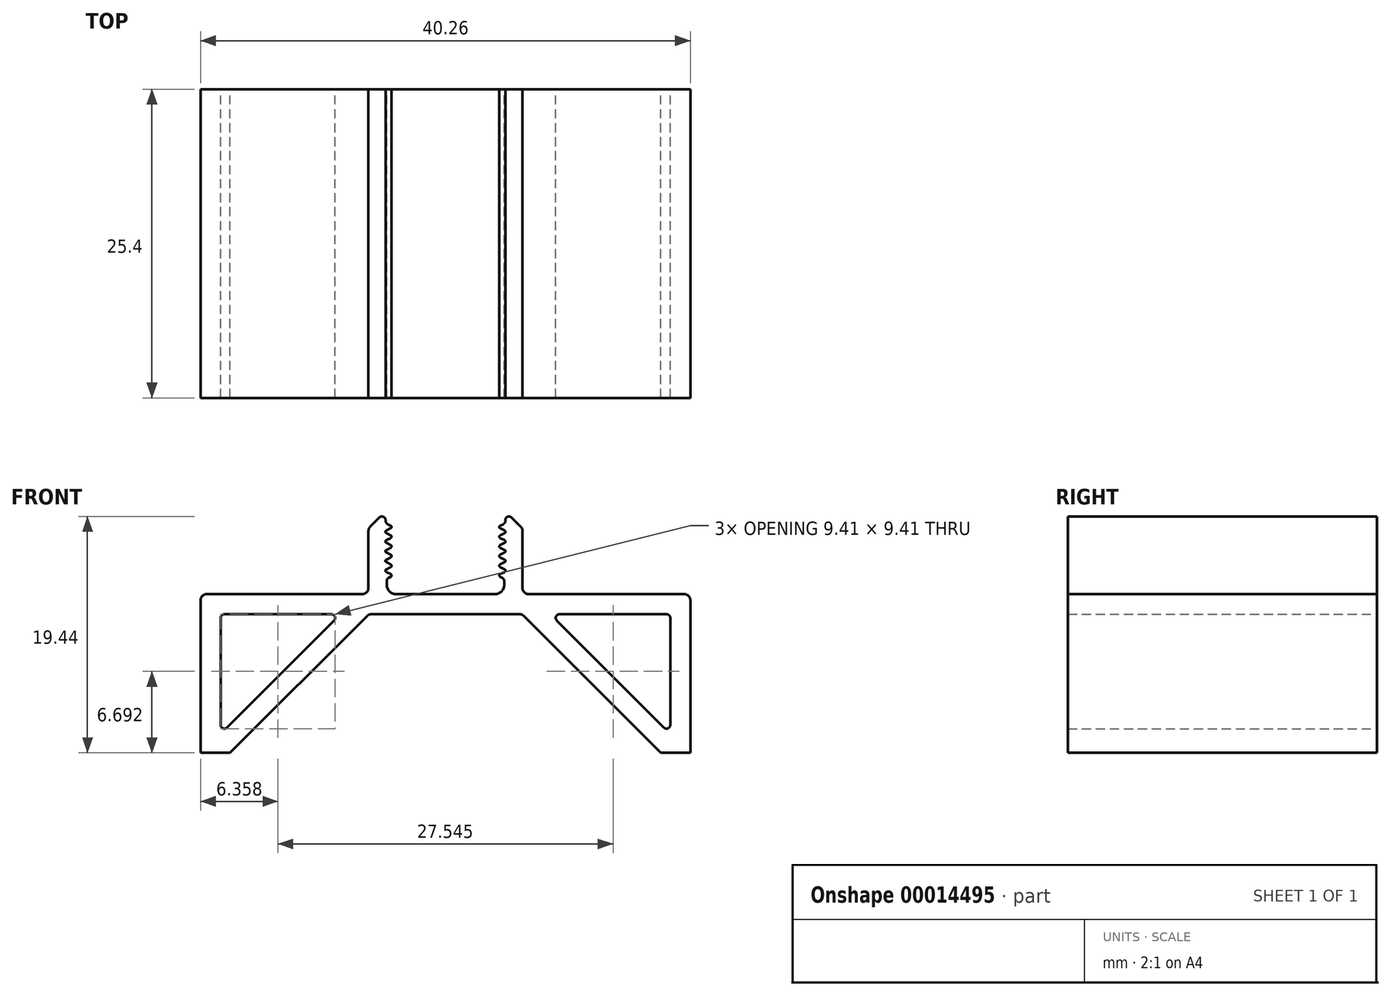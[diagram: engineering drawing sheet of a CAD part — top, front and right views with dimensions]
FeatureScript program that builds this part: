
annotation { "Feature Type Name" : "Feature", "Feature Type Description" : "" }
export const myFeature = defineFeature(function(context is Context, id is Id, definition is map)
    precondition{}
    {
        {
            var Q0;
            Q0=qCreatedBy(makeId("Front.planeOp"),FACE);
            var sketch = newSketch(context, id + "F0", { "sketchPlane" : qUnion([Q0])});
            skArc(sketch, "E0", {"start": v(4.43, 10.26) * mm, "mid": v(4.45, 10.2) * mm, "end": v(4.5, 10.15) * mm});
            skLineSegment(sketch, "E1", {"start": v(4.5, 10.15) * mm, "end": v(4.86, 9.97) * mm});
            skArc(sketch, "E2", {"start": v(4.86, 9.97) * mm, "mid": v(4.91, 9.92) * mm, "end": v(4.93, 9.86) * mm});
            skArc(sketch, "E3", {"start": v(4.93, 9.86) * mm, "mid": v(4.91, 9.8) * mm, "end": v(4.86, 9.75) * mm});
            skLineSegment(sketch, "E4", {"start": v(4.86, 9.75) * mm, "end": v(4.5, 9.57) * mm});
            skArc(sketch, "E5", {"start": v(4.5, 9.57) * mm, "mid": v(4.43, 9.46) * mm, "end": v(4.5, 9.35) * mm});
            skLineSegment(sketch, "E6", {"start": v(4.5, 9.35) * mm, "end": v(4.86, 9.17) * mm});
            skArc(sketch, "E7", {"start": v(4.86, 9.17) * mm, "mid": v(4.91, 9.12) * mm, "end": v(4.93, 9.06) * mm});
            skArc(sketch, "E8", {"start": v(4.93, 9.06) * mm, "mid": v(4.91, 9) * mm, "end": v(4.86, 8.95) * mm});
            skLineSegment(sketch, "E9", {"start": v(4.86, 8.95) * mm, "end": v(4.5, 8.77) * mm});
            skArc(sketch, "E10", {"start": v(4.5, 8.77) * mm, "mid": v(4.43, 8.66) * mm, "end": v(4.5, 8.56) * mm});
            skLineSegment(sketch, "E11", {"start": v(4.5, 8.56) * mm, "end": v(4.86, 8.37) * mm});
            skArc(sketch, "E12", {"start": v(4.86, 8.37) * mm, "mid": v(4.91, 8.33) * mm, "end": v(4.93, 8.26) * mm});
            skArc(sketch, "E13", {"start": v(4.93, 8.26) * mm, "mid": v(4.91, 8.2) * mm, "end": v(4.86, 8.16) * mm});
            skLineSegment(sketch, "E14", {"start": v(4.86, 8.16) * mm, "end": v(4.5, 7.97) * mm});
            skArc(sketch, "E15", {"start": v(4.5, 7.97) * mm, "mid": v(4.43, 7.86) * mm, "end": v(4.5, 7.76) * mm});
            skLineSegment(sketch, "E16", {"start": v(4.5, 7.76) * mm, "end": v(4.86, 7.57) * mm});
            skArc(sketch, "E17", {"start": v(4.86, 7.57) * mm, "mid": v(4.91, 7.53) * mm, "end": v(4.93, 7.47) * mm});
            skArc(sketch, "E18", {"start": v(4.93, 7.47) * mm, "mid": v(4.91, 7.4) * mm, "end": v(4.86, 7.36) * mm});
            skLineSegment(sketch, "E19", {"start": v(4.86, 7.36) * mm, "end": v(4.5, 7.17) * mm});
            skArc(sketch, "E20", {"start": v(4.5, 7.17) * mm, "mid": v(4.43, 7.07) * mm, "end": v(4.5, 6.96) * mm});
            skLineSegment(sketch, "E21", {"start": v(4.5, 6.96) * mm, "end": v(4.66, 6.88) * mm});
            skArc(sketch, "E22", {"start": v(4.66, 6.88) * mm, "mid": v(4.78, 6.77) * mm, "end": v(4.83, 6.6) * mm});
            skLineSegment(sketch, "E23", {"start": v(4.83, 6.6) * mm, "end": v(4.83, 6.3) * mm});
            skArc(sketch, "E24", {"start": v(4.83, 6.3) * mm, "mid": v(4.6, 5.75) * mm, "end": v(4.07, 5.53) * mm});
            skLineSegment(sketch, "E25", {"start": v(4.07, 5.53) * mm, "end": v(-4.07, 5.53) * mm});
            skArc(sketch, "E26", {"start": v(-4.07, 5.53) * mm, "mid": v(-4.6, 5.75) * mm, "end": v(-4.83, 6.3) * mm});
            skLineSegment(sketch, "E27", {"start": v(-4.83, 6.3) * mm, "end": v(-4.83, 6.6) * mm});
            skArc(sketch, "E28", {"start": v(-4.83, 6.6) * mm, "mid": v(-4.78, 6.77) * mm, "end": v(-4.66, 6.88) * mm});
            skLineSegment(sketch, "E29", {"start": v(-4.66, 6.88) * mm, "end": v(-4.5, 6.96) * mm});
            skArc(sketch, "E30", {"start": v(-4.5, 6.96) * mm, "mid": v(-4.43, 7.07) * mm, "end": v(-4.5, 7.17) * mm});
            skLineSegment(sketch, "E31", {"start": v(-4.5, 7.17) * mm, "end": v(-4.86, 7.36) * mm});
            skArc(sketch, "E32", {"start": v(-4.86, 7.36) * mm, "mid": v(-4.91, 7.4) * mm, "end": v(-4.93, 7.47) * mm});
            skArc(sketch, "E33", {"start": v(-4.93, 7.47) * mm, "mid": v(-4.91, 7.53) * mm, "end": v(-4.86, 7.57) * mm});
            skLineSegment(sketch, "E34", {"start": v(-4.86, 7.57) * mm, "end": v(-4.5, 7.76) * mm});
            skArc(sketch, "E35", {"start": v(-4.5, 7.76) * mm, "mid": v(-4.43, 7.86) * mm, "end": v(-4.5, 7.97) * mm});
            skLineSegment(sketch, "E36", {"start": v(-4.5, 7.97) * mm, "end": v(-4.86, 8.16) * mm});
            skArc(sketch, "E37", {"start": v(-4.86, 8.16) * mm, "mid": v(-4.91, 8.2) * mm, "end": v(-4.93, 8.26) * mm});
            skArc(sketch, "E38", {"start": v(-4.93, 8.26) * mm, "mid": v(-4.91, 8.33) * mm, "end": v(-4.86, 8.37) * mm});
            skLineSegment(sketch, "E39", {"start": v(-4.86, 8.37) * mm, "end": v(-4.5, 8.56) * mm});
            skArc(sketch, "E40", {"start": v(-4.5, 8.56) * mm, "mid": v(-4.43, 8.66) * mm, "end": v(-4.5, 8.77) * mm});
            skLineSegment(sketch, "E41", {"start": v(-4.5, 8.77) * mm, "end": v(-4.86, 8.95) * mm});
            skArc(sketch, "E42", {"start": v(-4.86, 8.95) * mm, "mid": v(-4.91, 9) * mm, "end": v(-4.93, 9.06) * mm});
            skArc(sketch, "E43", {"start": v(-4.93, 9.06) * mm, "mid": v(-4.91, 9.12) * mm, "end": v(-4.86, 9.17) * mm});
            skLineSegment(sketch, "E44", {"start": v(-4.86, 9.17) * mm, "end": v(-4.5, 9.35) * mm});
            skArc(sketch, "E45", {"start": v(-4.5, 9.35) * mm, "mid": v(-4.43, 9.46) * mm, "end": v(-4.5, 9.57) * mm});
            skLineSegment(sketch, "E46", {"start": v(-4.5, 9.57) * mm, "end": v(-4.86, 9.75) * mm});
            skArc(sketch, "E47", {"start": v(-4.86, 9.75) * mm, "mid": v(-4.91, 9.8) * mm, "end": v(-4.93, 9.86) * mm});
            skArc(sketch, "E48", {"start": v(-4.93, 9.86) * mm, "mid": v(-4.91, 9.92) * mm, "end": v(-4.86, 9.97) * mm});
            skLineSegment(sketch, "E49", {"start": v(-4.86, 9.97) * mm, "end": v(-4.5, 10.15) * mm});
            skArc(sketch, "E50", {"start": v(-4.5, 10.15) * mm, "mid": v(-4.43, 10.26) * mm, "end": v(-4.5, 10.36) * mm});
            skLineSegment(sketch, "E51", {"start": v(-4.5, 10.36) * mm, "end": v(-4.86, 10.55) * mm});
            skArc(sketch, "E52", {"start": v(-4.86, 10.55) * mm, "mid": v(-4.91, 10.6) * mm, "end": v(-4.93, 10.66) * mm});
            skArc(sketch, "E53", {"start": v(-4.93, 10.66) * mm, "mid": v(-4.91, 10.72) * mm, "end": v(-4.86, 10.76) * mm});
            skLineSegment(sketch, "E54", {"start": v(-4.86, 10.76) * mm, "end": v(-4.5, 10.95) * mm});
            skArc(sketch, "E55", {"start": v(-4.5, 10.95) * mm, "mid": v(-4.43, 11.06) * mm, "end": v(-4.5, 11.16) * mm});
            skLineSegment(sketch, "E56", {"start": v(-4.5, 11.16) * mm, "end": v(-4.76, 11.3) * mm});
            skArc(sketch, "E57", {"start": v(-4.76, 11.3) * mm, "mid": v(-4.88, 11.42) * mm, "end": v(-4.92, 11.6) * mm});
            skArc(sketch, "E58", {"start": v(-4.92, 11.6) * mm, "mid": v(-5.1, 11.9) * mm, "end": v(-5.44, 11.83) * mm});
            skLineSegment(sketch, "E59", {"start": v(-5.44, 11.83) * mm, "end": v(-6.18, 11.1) * mm});
            skArc(sketch, "E60", {"start": v(-6.18, 11.1) * mm, "mid": v(-6.29, 10.93) * mm, "end": v(-6.33, 10.74) * mm});
            skLineSegment(sketch, "E61", {"start": v(-6.33, 10.74) * mm, "end": v(-6.33, 6.04) * mm});
            skArc(sketch, "E62", {"start": v(-6.33, 6.04) * mm, "mid": v(-6.48, 5.68) * mm, "end": v(-6.83, 5.53) * mm});
            skLineSegment(sketch, "E63", {"start": v(-6.83, 5.53) * mm, "end": v(-19.62, 5.53) * mm});
            skArc(sketch, "E64", {"start": v(-19.62, 5.53) * mm, "mid": v(-19.98, 5.38) * mm, "end": v(-20.13, 5.02) * mm});
            skLineSegment(sketch, "E65", {"start": v(-20.13, 5.02) * mm, "end": v(-20.13, -9.96) * mm});
            skArc(sketch, "E66", {"start": v(-20.13, -9.96) * mm, "mid": v(-20.22, -10.18) * mm, "end": v(-20.43, -10.27) * mm});
            skLineSegment(sketch, "E67", {"start": v(-20.43, -10.27) * mm, "end": v(-20.57, -10.27) * mm});
            skArc(sketch, "E68", {"start": v(-20.57, -10.27) * mm, "mid": v(-20.72, -10.23) * mm, "end": v(-20.83, -10.12) * mm});
            skLineSegment(sketch, "E69", {"start": v(-20.83, -10.12) * mm, "end": v(-21.34, -9.23) * mm});
            skArc(sketch, "E70", {"start": v(-21.34, -9.23) * mm, "mid": v(-21.46, -9.12) * mm, "end": v(-21.6, -9.08) * mm});
            skLineSegment(sketch, "E71", {"start": v(-21.6, -9.08) * mm, "end": v(-22.5, -9.08) * mm});
            skArc(sketch, "E72", {"start": v(-22.5, -9.08) * mm, "mid": v(-22.7, -9.17) * mm, "end": v(-22.8, -9.38) * mm});
            skLineSegment(sketch, "E73", {"start": v(-22.8, -9.38) * mm, "end": v(-22.8, -9.88) * mm});
            skArc(sketch, "E74", {"start": v(-22.8, -9.88) * mm, "mid": v(-22.78, -10.01) * mm, "end": v(-22.73, -10.13) * mm});
            skLineSegment(sketch, "E75", {"start": v(-22.73, -10.13) * mm, "end": v(-21.84, -11.67) * mm});
            skArc(sketch, "E76", {"start": v(-21.84, -11.67) * mm, "mid": v(-21.66, -11.85) * mm, "end": v(-21.4, -11.92) * mm});
            skLineSegment(sketch, "E77", {"start": v(-21.4, -11.92) * mm, "end": v(-16.75, -11.92) * mm});
            skArc(sketch, "E78", {"start": v(-16.75, -11.92) * mm, "mid": v(-16.4, -11.77) * mm, "end": v(-16.24, -11.41) * mm});
            skLineSegment(sketch, "E79", {"start": v(-16.24, -11.41) * mm, "end": v(-16.24, -10.78) * mm});
            skArc(sketch, "E80", {"start": v(-16.24, -10.78) * mm, "mid": v(-16.4, -10.42) * mm, "end": v(-16.75, -10.27) * mm});
            skLineSegment(sketch, "E81", {"start": v(-16.75, -10.27) * mm, "end": v(-17.97, -10.27) * mm});
            skArc(sketch, "E82", {"start": v(-17.97, -10.27) * mm, "mid": v(-18.33, -10.12) * mm, "end": v(-18.48, -9.76) * mm});
            skLineSegment(sketch, "E83", {"start": v(-18.48, -9.76) * mm, "end": v(-18.48, -8.51) * mm});
            skArc(sketch, "E84", {"start": v(-18.48, -8.51) * mm, "mid": v(-18.44, -8.32) * mm, "end": v(-18.33, -8.15) * mm});
            skLineSegment(sketch, "E85", {"start": v(-18.33, -8.15) * mm, "end": v(-6.45, 3.73) * mm});
            skArc(sketch, "E86", {"start": v(-6.45, 3.73) * mm, "mid": v(-6.28, 3.84) * mm, "end": v(-6.09, 3.88) * mm});
            skLineSegment(sketch, "E87", {"start": v(-6.09, 3.88) * mm, "end": v(6.09, 3.88) * mm});
            skArc(sketch, "E88", {"start": v(6.09, 3.88) * mm, "mid": v(6.28, 3.84) * mm, "end": v(6.45, 3.73) * mm});
            skLineSegment(sketch, "E89", {"start": v(6.45, 3.73) * mm, "end": v(18.33, -8.15) * mm});
            skArc(sketch, "E90", {"start": v(18.33, -8.15) * mm, "mid": v(18.44, -8.32) * mm, "end": v(18.48, -8.51) * mm});
            skLineSegment(sketch, "E91", {"start": v(18.48, -8.51) * mm, "end": v(18.48, -9.76) * mm});
            skArc(sketch, "E92", {"start": v(18.48, -9.76) * mm, "mid": v(18.33, -10.12) * mm, "end": v(17.97, -10.27) * mm});
            skLineSegment(sketch, "E93", {"start": v(17.97, -10.27) * mm, "end": v(16.75, -10.27) * mm});
            skArc(sketch, "E94", {"start": v(16.75, -10.27) * mm, "mid": v(16.4, -10.42) * mm, "end": v(16.24, -10.78) * mm});
            skLineSegment(sketch, "E95", {"start": v(16.24, -10.78) * mm, "end": v(16.24, -11.41) * mm});
            skArc(sketch, "E96", {"start": v(16.24, -11.41) * mm, "mid": v(16.4, -11.77) * mm, "end": v(16.75, -11.92) * mm});
            skLineSegment(sketch, "E97", {"start": v(16.75, -11.92) * mm, "end": v(21.4, -11.92) * mm});
            skArc(sketch, "E98", {"start": v(21.4, -11.92) * mm, "mid": v(21.66, -11.85) * mm, "end": v(21.84, -11.67) * mm});
            skLineSegment(sketch, "E99", {"start": v(21.84, -11.67) * mm, "end": v(22.73, -10.13) * mm});
            skArc(sketch, "E100", {"start": v(22.73, -10.13) * mm, "mid": v(22.78, -10.01) * mm, "end": v(22.8, -9.88) * mm});
            skLineSegment(sketch, "E101", {"start": v(22.8, -9.88) * mm, "end": v(22.8, -9.38) * mm});
            skArc(sketch, "E102", {"start": v(22.8, -9.38) * mm, "mid": v(22.7, -9.17) * mm, "end": v(22.5, -9.08) * mm});
            skLineSegment(sketch, "E103", {"start": v(22.5, -9.08) * mm, "end": v(21.6, -9.08) * mm});
            skArc(sketch, "E104", {"start": v(21.6, -9.08) * mm, "mid": v(21.46, -9.12) * mm, "end": v(21.34, -9.23) * mm});
            skLineSegment(sketch, "E105", {"start": v(21.34, -9.23) * mm, "end": v(20.83, -10.12) * mm});
            skArc(sketch, "E106", {"start": v(20.83, -10.12) * mm, "mid": v(20.72, -10.23) * mm, "end": v(20.57, -10.27) * mm});
            skLineSegment(sketch, "E107", {"start": v(20.57, -10.27) * mm, "end": v(20.43, -10.27) * mm});
            skArc(sketch, "E108", {"start": v(20.43, -10.27) * mm, "mid": v(20.22, -10.18) * mm, "end": v(20.13, -9.96) * mm});
            skLineSegment(sketch, "E109", {"start": v(20.13, -9.96) * mm, "end": v(20.13, 5.02) * mm});
            skArc(sketch, "E110", {"start": v(20.13, 5.02) * mm, "mid": v(19.98, 5.38) * mm, "end": v(19.62, 5.53) * mm});
            skLineSegment(sketch, "E111", {"start": v(19.62, 5.53) * mm, "end": v(6.83, 5.53) * mm});
            skArc(sketch, "E112", {"start": v(6.83, 5.53) * mm, "mid": v(6.48, 5.68) * mm, "end": v(6.33, 6.04) * mm});
            skLineSegment(sketch, "E113", {"start": v(6.33, 6.04) * mm, "end": v(6.33, 10.74) * mm});
            skArc(sketch, "E114", {"start": v(6.33, 10.74) * mm, "mid": v(6.29, 10.93) * mm, "end": v(6.18, 11.1) * mm});
            skLineSegment(sketch, "E115", {"start": v(6.18, 11.1) * mm, "end": v(5.44, 11.83) * mm});
            skArc(sketch, "E116", {"start": v(5.44, 11.83) * mm, "mid": v(5.1, 11.9) * mm, "end": v(4.92, 11.6) * mm});
            skArc(sketch, "E117", {"start": v(4.92, 11.6) * mm, "mid": v(4.88, 11.42) * mm, "end": v(4.76, 11.3) * mm});
            skLineSegment(sketch, "E118", {"start": v(4.76, 11.3) * mm, "end": v(4.5, 11.16) * mm});
            skArc(sketch, "E119", {"start": v(4.5, 11.16) * mm, "mid": v(4.43, 11.06) * mm, "end": v(4.5, 10.95) * mm});
            skLineSegment(sketch, "E120", {"start": v(4.5, 10.95) * mm, "end": v(4.86, 10.76) * mm});
            skArc(sketch, "E121", {"start": v(4.86, 10.76) * mm, "mid": v(4.91, 10.72) * mm, "end": v(4.93, 10.66) * mm});
            skArc(sketch, "E122", {"start": v(4.93, 10.66) * mm, "mid": v(4.91, 10.6) * mm, "end": v(4.86, 10.55) * mm});
            skLineSegment(sketch, "E123", {"start": v(4.86, 10.55) * mm, "end": v(4.5, 10.36) * mm});
            skArc(sketch, "E124", {"start": v(4.5, 10.36) * mm, "mid": v(4.43, 10.26) * mm, "end": v(4.5, 10.15) * mm});
            skArc(sketch, "E125", {"start": v(-4.43, 10.26) * mm, "mid": v(-4.45, 10.2) * mm, "end": v(-4.5, 10.15) * mm});
            skLineSegment(sketch, "E126", {"start": v(-18.48, -5.23) * mm, "end": v(-18.48, 3.57) * mm});
            skArc(sketch, "E127", {"start": v(-18.48, 3.57) * mm, "mid": v(-18.39, 3.79) * mm, "end": v(-18.17, 3.88) * mm});
            skLineSegment(sketch, "E128", {"start": v(-18.17, 3.88) * mm, "end": v(-9.37, 3.88) * mm});
            skArc(sketch, "E129", {"start": v(-9.37, 3.88) * mm, "mid": v(-9.09, 3.69) * mm, "end": v(-9.15, 3.36) * mm});
            skLineSegment(sketch, "E130", {"start": v(-9.15, 3.36) * mm, "end": v(-17.96, -5.45) * mm});
            skArc(sketch, "E131", {"start": v(-17.96, -5.45) * mm, "mid": v(-18.3, -5.51) * mm, "end": v(-18.48, -5.23) * mm});
            skArc(sketch, "E132", {"start": v(18.48, -5.23) * mm, "mid": v(18.3, -5.51) * mm, "end": v(17.96, -5.45) * mm});
            skLineSegment(sketch, "E133", {"start": v(17.96, -5.45) * mm, "end": v(9.15, 3.36) * mm});
            skArc(sketch, "E134", {"start": v(9.15, 3.36) * mm, "mid": v(9.09, 3.69) * mm, "end": v(9.37, 3.88) * mm});
            skLineSegment(sketch, "E135", {"start": v(9.37, 3.88) * mm, "end": v(18.17, 3.88) * mm});
            skArc(sketch, "E136", {"start": v(18.17, 3.88) * mm, "mid": v(18.39, 3.79) * mm, "end": v(18.48, 3.57) * mm});
            skLineSegment(sketch, "E137", {"start": v(18.48, 3.57) * mm, "end": v(18.48, -5.23) * mm});
            skLineSegment(sketch, "E138", {"start": v(20.13, -7.52) * mm, "end": v(-20.13, -7.52) * mm});
            skSolve(sketch);
        }
        {
            var Q0;
            Q0=makeQuery(id+"F0.imprint","IMPRINT",FACE,{"disambiguationData":[TD([[makeQuery(id+"F0.imprint","IMPRINT",EDGE,{"derivedFrom":sQuery(id+"F0.wireOp",EDGE,"E126")}),-1.0]])]});
            var Q1;
            Q1=makeQuery(id+"F0.imprint","IMPRINT",FACE,{"disambiguationData":[TD([[makeQuery(id+"F0.imprint","IMPRINT",EDGE,{"derivedFrom":sQuery(id+"F0.wireOp",EDGE,"E132")}),-1.0]])]});
            var Q2;
            Q2=sQuery(id+"F0.wireOp",EDGE,"E126");
            var Q3;
            Q3=sQuery(id+"F0.wireOp",EDGE,"E63");
            var Q4;
            Q4=sQuery(id+"F0.wireOp",EDGE,"E111");
            var Q5;
            Q5=sQuery(id+"F0.wireOp",EDGE,"E85");
            var Q6;
            Q6=sQuery(id+"F0.wireOp",EDGE,"E133");
            var Q7;
            Q7=sQuery(id+"F0.wireOp",EDGE,"E87");
            var Q8;
            Q8=sQuery(id+"F0.wireOp",EDGE,"E135");
            var Q9;
            Q9=sQuery(id+"F0.wireOp",EDGE,"E128");
            var Q10;
            Q10=sQuery(id+"F0.wireOp",EDGE,"E25");
            var Q11;
            Q11=sQuery(id+"F0.wireOp",EDGE,"E89");
            var Q12;
            Q12=sQuery(id+"F0.wireOp",EDGE,"E137");
            var Q13;
            Q13=sQuery(id+"F0.wireOp",EDGE,"E113");
            var Q14;
            Q14=sQuery(id+"F0.wireOp",EDGE,"E77");
            var Q15;
            Q15=sQuery(id+"F0.wireOp",EDGE,"E61");
            var Q16;
            Q16=sQuery(id+"F0.wireOp",EDGE,"E65");
            var Q17;
            Q17=sQuery(id+"F0.wireOp",EDGE,"E97");
            var Q18;
            Q18=sQuery(id+"F0.wireOp",EDGE,"E109");
            var Q19;
            Q19=sQuery(id+"F0.wireOp",EDGE,"E130");
            var Q20;
            Q20=sQuery(id+"F0.wireOp",EDGE,"E76");
            var Q21;
            Q21=sQuery(id+"F0.wireOp",EDGE,"E92");
            var Q22;
            Q22=sQuery(id+"F0.wireOp",EDGE,"E83");
            var Q23;
            Q23=sQuery(id+"F0.wireOp",EDGE,"E99");
            var Q24;
            Q24=sQuery(id+"F0.wireOp",EDGE,"E78");
            var Q25;
            Q25=sQuery(id+"F0.wireOp",EDGE,"E62");
            var Q26;
            Q26=sQuery(id+"F0.wireOp",EDGE,"E110");
            var Q27;
            Q27=sQuery(id+"F0.wireOp",EDGE,"E79");
            var Q28;
            Q28=sQuery(id+"F0.wireOp",EDGE,"E86");
            var Q29;
            Q29=sQuery(id+"F0.wireOp",EDGE,"E134");
            var Q30;
            Q30=sQuery(id+"F0.wireOp",EDGE,"E24");
            var Q31;
            Q31=sQuery(id+"F0.wireOp",EDGE,"E112");
            var Q32;
            Q32=sQuery(id+"F0.wireOp",EDGE,"E105");
            var Q33;
            Q33=sQuery(id+"F0.wireOp",EDGE,"E80");
            var Q34;
            Q34=sQuery(id+"F0.wireOp",EDGE,"E26");
            var Q35;
            Q35=sQuery(id+"F0.wireOp",EDGE,"E90");
            var Q36;
            Q36=sQuery(id+"F0.wireOp",EDGE,"E81");
            var Q37;
            Q37=sQuery(id+"F0.wireOp",EDGE,"E91");
            var Q38;
            Q38=sQuery(id+"F0.wireOp",EDGE,"E75");
            var Q39;
            Q39=sQuery(id+"F0.wireOp",EDGE,"E93");
            var Q40;
            Q40=sQuery(id+"F0.wireOp",EDGE,"E82");
            var Q41;
            Q41=sQuery(id+"F0.wireOp",EDGE,"E98");
            var Q42;
            Q42=sQuery(id+"F0.wireOp",EDGE,"E60");
            var Q43;
            Q43=sQuery(id+"F0.wireOp",EDGE,"E131");
            var Q44;
            Q44=sQuery(id+"F0.wireOp",EDGE,"E115");
            var Q45;
            Q45=sQuery(id+"F0.wireOp",EDGE,"E94");
            var Q46;
            Q46=sQuery(id+"F0.wireOp",EDGE,"E84");
            var Q47;
            Q47=sQuery(id+"F0.wireOp",EDGE,"E132");
            var Q48;
            Q48=sQuery(id+"F0.wireOp",EDGE,"E116");
            var Q49;
            Q49=sQuery(id+"F0.wireOp",EDGE,"E100");
            var Q50;
            Q50=sQuery(id+"F0.wireOp",EDGE,"E127");
            var Q51;
            Q51=sQuery(id+"F0.wireOp",EDGE,"E95");
            var Q52;
            Q52=sQuery(id+"F0.wireOp",EDGE,"E117");
            var Q53;
            Q53=sQuery(id+"F0.wireOp",EDGE,"E101");
            var Q54;
            Q54=sQuery(id+"F0.wireOp",EDGE,"E102");
            var Q55;
            Q55=sQuery(id+"F0.wireOp",EDGE,"E103");
            var Q56;
            Q56=sQuery(id+"F0.wireOp",EDGE,"E104");
            var Q57;
            Q57=sQuery(id+"F0.wireOp",EDGE,"E96");
            var Q58;
            Q58=sQuery(id+"F0.wireOp",EDGE,"E64");
            var Q59;
            Q59=sQuery(id+"F0.wireOp",EDGE,"E129");
            var Q60;
            Q60=sQuery(id+"F0.wireOp",EDGE,"E27");
            var Q61;
            Q61=sQuery(id+"F0.wireOp",EDGE,"E59");
            var Q62;
            Q62=sQuery(id+"F0.wireOp",EDGE,"E114");
            var Q63;
            Q63=sQuery(id+"F0.wireOp",EDGE,"E108");
            var Q64;
            Q64=sQuery(id+"F0.wireOp",EDGE,"E71");
            var Q65;
            Q65=sQuery(id+"F0.wireOp",EDGE,"E88");
            var Q66;
            Q66=sQuery(id+"F0.wireOp",EDGE,"E136");
            var Q67;
            Q67=sQuery(id+"F0.wireOp",EDGE,"E72");
            var Q68;
            Q68=sQuery(id+"F0.wireOp",EDGE,"E73");
            var Q69;
            Q69=sQuery(id+"F0.wireOp",EDGE,"E106");
            var Q70;
            Q70=sQuery(id+"F0.wireOp",EDGE,"E74");
            var Q71;
            Q71=sQuery(id+"F0.wireOp",EDGE,"E107");
            var Q72;
            Q72=sQuery(id+"F0.wireOp",EDGE,"E68");
            var Q73;
            Q73=sQuery(id+"F0.wireOp",EDGE,"E69");
            var Q74;
            Q74=sQuery(id+"F0.wireOp",EDGE,"E70");
            var Q75;
            Q75=sQuery(id+"F0.wireOp",EDGE,"E118");
            var Q76;
            Q76=sQuery(id+"F0.wireOp",EDGE,"E23");
            var Q77;
            Q77=sQuery(id+"F0.wireOp",EDGE,"E58");
            var Q78;
            Q78=sQuery(id+"F0.wireOp",EDGE,"E66");
            var Q79;
            Q79=sQuery(id+"F0.wireOp",EDGE,"E28");
            var Q80;
            Q80=sQuery(id+"F0.wireOp",EDGE,"E67");
            var Q81;
            Q81=sQuery(id+"F0.wireOp",EDGE,"E56");
            var Q82;
            Q82=sQuery(id+"F0.wireOp",EDGE,"E120");
            var Q83;
            Q83=sQuery(id+"F0.wireOp",EDGE,"E57");
            var Q84;
            Q84=sQuery(id+"F0.wireOp",EDGE,"E121");
            var Q85;
            Q85=sQuery(id+"F0.wireOp",EDGE,"E22");
            var Q86;
            Q86=sQuery(id+"F0.wireOp",EDGE,"E55");
            var Q87;
            Q87=sQuery(id+"F0.wireOp",EDGE,"E119");
            var Q88;
            Q88=sQuery(id+"F0.wireOp",EDGE,"E21");
            var Q89;
            Q89=sQuery(id+"F0.wireOp",EDGE,"E124");
            var Q90;
            Q90=sQuery(id+"F0.wireOp",EDGE,"E19");
            var Q91;
            Q91=sQuery(id+"F0.wireOp",EDGE,"E30");
            var Q92;
            Q92=sQuery(id+"F0.wireOp",EDGE,"E20");
            var Q93;
            Q93=sQuery(id+"F0.wireOp",EDGE,"E1");
            var Q94;
            Q94=sQuery(id+"F0.wireOp",EDGE,"E3");
            var Q95;
            Q95=sQuery(id+"F0.wireOp",EDGE,"E4");
            var Q96;
            Q96=sQuery(id+"F0.wireOp",EDGE,"E5");
            var Q97;
            Q97=sQuery(id+"F0.wireOp",EDGE,"E16");
            var Q98;
            Q98=sQuery(id+"F0.wireOp",EDGE,"E32");
            var Q99;
            Q99=sQuery(id+"F0.wireOp",EDGE,"E123");
            var Q100;
            Q100=sQuery(id+"F0.wireOp",EDGE,"E29");
            var Q101;
            Q101=sQuery(id+"F0.wireOp",EDGE,"E18");
            var Q102;
            Q102=sQuery(id+"F0.wireOp",EDGE,"E31");
            var Q103;
            Q103=sQuery(id+"F0.wireOp",EDGE,"E14");
            var Q104;
            Q104=sQuery(id+"F0.wireOp",EDGE,"E15");
            var Q105;
            Q105=sQuery(id+"F0.wireOp",EDGE,"E0");
            var Q106;
            Q106=sQuery(id+"F0.wireOp",EDGE,"E2");
            var Q107;
            Q107=sQuery(id+"F0.wireOp",EDGE,"E6");
            var Q108;
            Q108=sQuery(id+"F0.wireOp",EDGE,"E8");
            var Q109;
            Q109=sQuery(id+"F0.wireOp",EDGE,"E9");
            var Q110;
            Q110=sQuery(id+"F0.wireOp",EDGE,"E10");
            var Q111;
            Q111=sQuery(id+"F0.wireOp",EDGE,"E11");
            var Q112;
            Q112=sQuery(id+"F0.wireOp",EDGE,"E12");
            var Q113;
            Q113=sQuery(id+"F0.wireOp",EDGE,"E122");
            var Q114;
            Q114=sQuery(id+"F0.wireOp",EDGE,"E17");
            var Q115;
            Q115=sQuery(id+"F0.wireOp",EDGE,"E33");
            var Q116;
            Q116=sQuery(id+"F0.wireOp",EDGE,"E34");
            var Q117;
            Q117=sQuery(id+"F0.wireOp",EDGE,"E35");
            var Q118;
            Q118=sQuery(id+"F0.wireOp",EDGE,"E13");
            var Q119;
            Q119=sQuery(id+"F0.wireOp",EDGE,"E7");
            var Q120;
            Q120=sQuery(id+"F0.wireOp",EDGE,"E44");
            var Q121;
            Q121=sQuery(id+"F0.wireOp",EDGE,"E36");
            var Q122;
            Q122=sQuery(id+"F0.wireOp",EDGE,"E39");
            var Q123;
            Q123=sQuery(id+"F0.wireOp",EDGE,"E41");
            var Q124;
            Q124=sQuery(id+"F0.wireOp",EDGE,"E42");
            var Q125;
            Q125=sQuery(id+"F0.wireOp",EDGE,"E43");
            var Q126;
            Q126=sQuery(id+"F0.wireOp",EDGE,"E46");
            var Q127;
            Q127=sQuery(id+"F0.wireOp",EDGE,"E52");
            var Q128;
            Q128=sQuery(id+"F0.wireOp",EDGE,"E53");
            var Q129;
            Q129=sQuery(id+"F0.wireOp",EDGE,"E38");
            var Q130;
            Q130=sQuery(id+"F0.wireOp",EDGE,"E54");
            var Q131;
            Q131=sQuery(id+"F0.wireOp",EDGE,"E40");
            var Q132;
            Q132=sQuery(id+"F0.wireOp",EDGE,"E48");
            var Q133;
            Q133=sQuery(id+"F0.wireOp",EDGE,"E49");
            var Q134;
            Q134=sQuery(id+"F0.wireOp",EDGE,"E45");
            var Q135;
            Q135=sQuery(id+"F0.wireOp",EDGE,"E50");
            var Q136;
            Q136=sQuery(id+"F0.wireOp",EDGE,"E51");
            var Q137;
            Q137=sQuery(id+"F0.wireOp",EDGE,"E47");
            var Q138;
            Q138=sQuery(id+"F0.wireOp",EDGE,"E37");
            var Q139;
            Q139=sQuery(id+"F0.wireOp",EDGE,"E125");
            extrude(context, id + "F1", {"entities" : qUnion([Q0, Q1]), "surfaceEntities" : qUnion([Q2, Q3, Q4, Q5, Q6, Q7, Q8, Q9, Q10, Q11, Q12, Q13, Q14, Q15, Q16, Q17, Q18, Q19, Q20, Q21, Q22, Q23, Q24, Q25, Q26, Q27, Q28, Q29, Q30, Q31, Q32, Q33, Q34, Q35, Q36, Q37, Q38, Q39, Q40, Q41, Q42, Q43, Q44, Q45, Q46, Q47, Q48, Q49, Q50, Q51, Q52, Q53, Q54, Q55, Q56, Q57, Q58, Q59, Q60, Q61, Q62, Q63, Q64, Q65, Q66, Q67, Q68, Q69, Q70, Q71, Q72, Q73, Q74, Q75, Q76, Q77, Q78, Q79, Q80, Q81, Q82, Q83, Q84, Q85, Q86, Q87, Q88, Q89, Q90, Q91, Q92, Q93, Q94, Q95, Q96, Q97, Q98, Q99, Q100, Q101, Q102, Q103, Q104, Q105, Q106, Q107, Q108, Q109, Q110, Q111, Q112, Q113, Q114, Q115, Q116, Q117, Q118, Q119, Q120, Q121, Q122, Q123, Q124, Q125, Q126, Q127, Q128, Q129, Q130, Q131, Q132, Q133, Q134, Q135, Q136, Q137, Q138, Q139]), "depth" : 25.4 * mm});
        }
        {
            var Q0;
            {var subQ15=sQuery(id+"F0.wireOp",EDGE,"E1");Q0=makeQuery(id+"F0.imprint","IMPRINT",FACE,{"disambiguationData":[TD([[makeQuery(id+"F0.imprint","IMPRINT",EDGE,{"derivedFrom":subQ15}),1.0]])]});}
            extrude(context, id + "F2", {"entities" : qUnion([Q0]), "depth" : 25.4 * mm});
        }
    });
